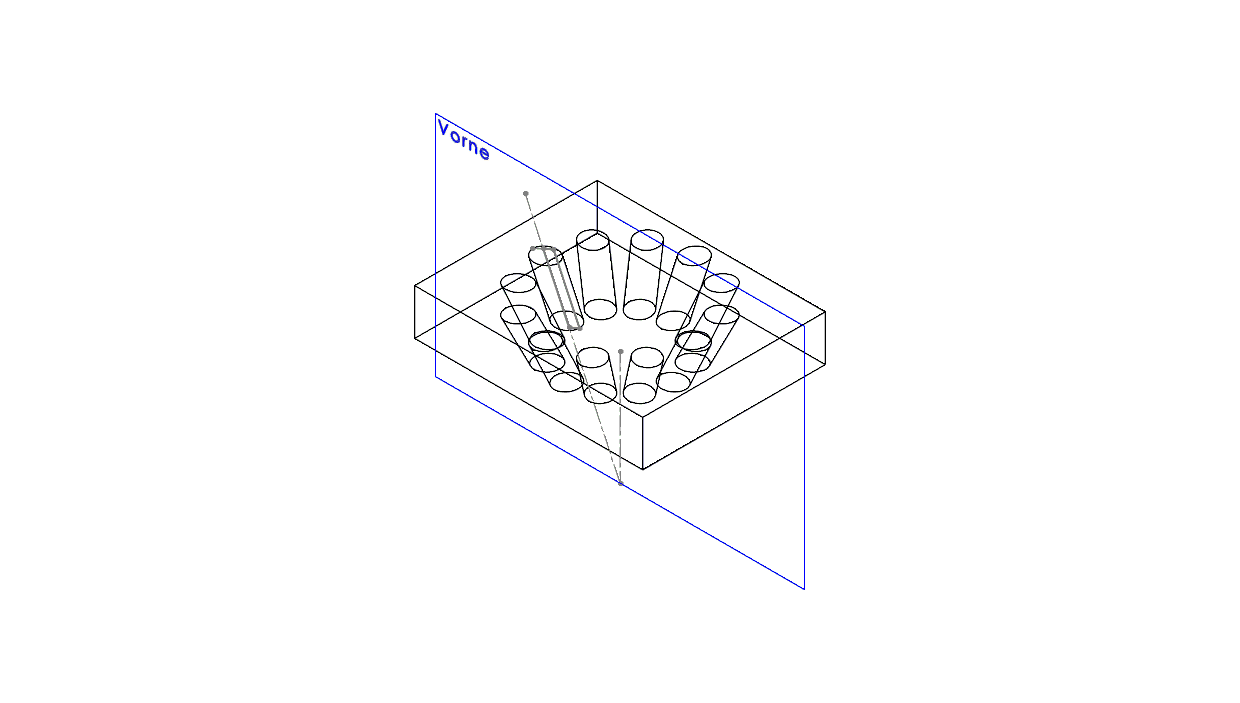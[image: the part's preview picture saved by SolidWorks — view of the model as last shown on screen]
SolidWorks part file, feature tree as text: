
SOLIDWORKS PART (.sldprt)
format: sldprt  version: not decoded by parser v0  size: 196,608 bytes
history: native  units: mm
features: plane x3, sketch x2, material x1, extrude x1, cut_revolve x1, pattern_circular x1 (+8 scaffold rows collapsed)
feature tree (17):
  scaffold x8  (default folders/planes/origin — collapsed)
  material  "Material <nicht festgelegt>"
  plane  "Vorne"
  plane  "Oben"
  plane  "Rechts"
  sketch  "Skizze1"  dims[c1.D1=~98.034611mm c2.D1=100.0mm c2.D2=80.0mm]
  extrude  "Aufsatz-Linear austragen1"  Depth=20mm
  sketch  "Skizze2"  dims[c1.D1=~88.936598mm c2.D1=25.0deg c2.D2=~57.396298mm c3.D2=50.0mm c3.D3=~31.675387mm c4.D3=10.0mm c4.D4=50.0mm]
  cut_revolve  "Schnitt-Rotation1"  Angle=360deg
  pattern_circular  "Kreismuster1"  Count=12 Angle=360deg
decode coverage: 5 of 5 modeling features carry decoded parameters
note: ~ marks probable driven/reference dimensions
note: suppression state not decoded; provenance and decode notes live in map.json
